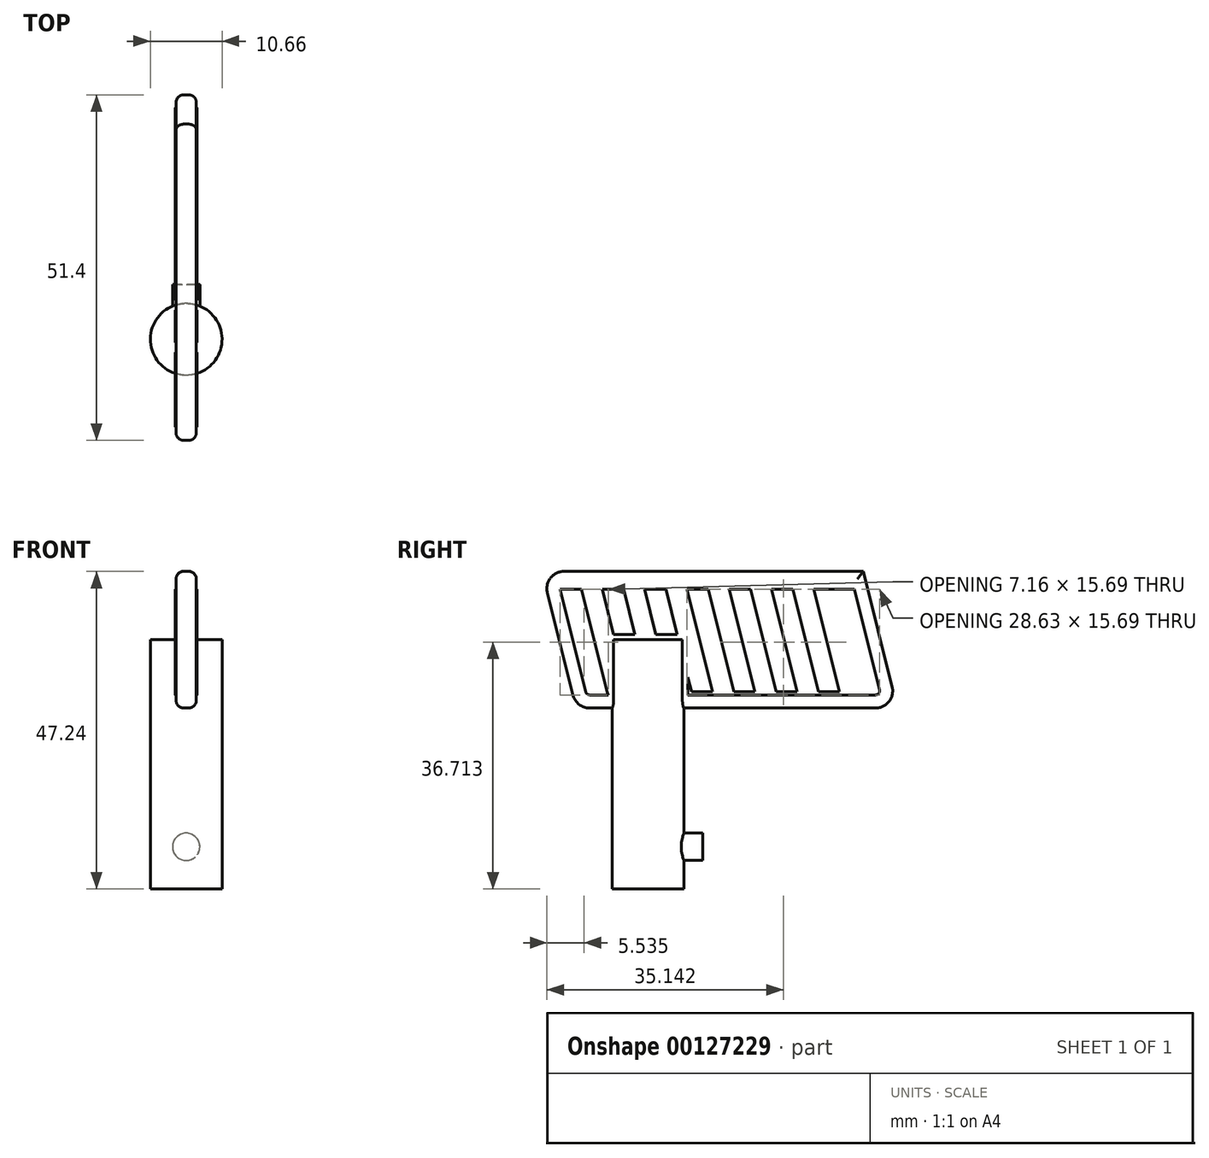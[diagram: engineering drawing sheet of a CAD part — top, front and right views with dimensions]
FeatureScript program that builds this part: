
annotation { "Feature Type Name" : "Feature", "Feature Type Description" : "" }
export const myFeature = defineFeature(function(context is Context, id is Id, definition is map)
    precondition{}
    {
        {
            var Q0;
            Q0=qCreatedBy(makeId("Top.planeOp"),FACE);
            var sketch = newSketch(context, id + "F0", { "sketchPlane" : qUnion([Q0])});
            skCircle(sketch, "E0", {"center": v(0, 0) * mm, "radius": 5.33 * mm});
            skSolve(sketch);
        }
        {
            var Q0;
            Q0 = qSketchRegion(id + "F0", true);
            extrude(context, id + "F1", {"entities" : qUnion([Q0]), "depth" : 37.08 * mm});
        }
        {
            var Q0;
            Q0=qCreatedBy(makeId("Front.planeOp"),FACE);
            var sketch = newSketch(context, id + "F2", { "sketchPlane" : qUnion([Q0])});
            skCircle(sketch, "E1", {"center": v(0, 6.27) * mm, "radius": 2.03 * mm});
            skSolve(sketch);
        }
        {
            var Q0;
            Q0 = qSketchRegion(id + "F2", true);
            extrude(context, id + "F3", {"entities" : qUnion([Q0]), "operationType" : NewBodyOperationType.ADD, "oppositeDirection" : true, "depth" : 8.13 * mm});
        }
        {
            var Q0;
            Q0=makeQuery(id+"F1.opExtrude","CAP_FACE",FACE,{"disambiguationData":[OSD([sQuery(id+"F0.wireOp",EDGE,"E0")])],"isStart":false});
            var sketch = newSketch(context, id + "F4", { "sketchPlane" : qUnion([Q0])});
            skLineSegment(sketch, "E2.bottom", {"start": v(-1.51, -10.67) * mm, "end": v(1.51, -10.67) * mm});
            skLineSegment(sketch, "E2.top", {"start": v(-1.51, 37.08) * mm, "end": v(1.51, 37.08) * mm});
            skLineSegment(sketch, "E2.left", {"start": v(-1.51, -10.67) * mm, "end": v(-1.51, 37.08) * mm});
            skLineSegment(sketch, "E2.right", {"start": v(1.51, -10.67) * mm, "end": v(1.51, 37.08) * mm});
            skSolve(sketch);
        }
        {
            var Q0;
            Q0 = qSketchRegion(id + "F4", true);
            extrude(context, id + "F5", {"entities" : qUnion([Q0]), "operationType" : NewBodyOperationType.ADD, "endBound" : BoundingType.SYMMETRIC, "depth" : 20.32 * mm});
        }
        {
            var Q0;
            Q0=makeQuery(id+"F5.opExtrude","SWEPT_FACE",FACE,{"disambiguationData":[OSD([sQuery(id+"F4.wireOp",EDGE,"E2.left")])]});
            var sketch = newSketch(context, id + "F6", { "sketchPlane" : qUnion([Q0])});
            skLineSegment(sketch, "E3", {"start": v(-37.08, 26.92) * mm, "end": v(-32, 47.24) * mm});
            skLineSegment(sketch, "E4", {"start": v(10.67, 26.92) * mm, "end": v(15.75, 47.24) * mm});
            skLineSegment(sketch, "E5", {"start": v(15.75, 47.24) * mm, "end": v(10.67, 47.24) * mm});
            skSolve(sketch);
        }
        {
            var Q0;
            Q0=makeQuery(id+"F6.imprint","IMPRINT",FACE,{"disambiguationData":[TD([[makeQuery(id+"F6.imprint","IMPRINT",EDGE,{"derivedFrom":sQuery(id+"F6.wireOp",EDGE,"E4")}),1.0]])]});
            var Q1;
            {var subQ0=sQuery(id+"F6.wireOp",EDGE,"E3");Q1=makeQuery(id+"F6.imprint","IMPRINT",FACE,{"disambiguationData":[TD([[makeQuery(id+"F6.imprint","IMPRINT",EDGE,{"derivedFrom":subQ0}),1.0]])]});}
            extrude(context, id + "F7", {"entities" : qUnion([Q0, Q1]), "operationType" : NewBodyOperationType.ADD, "oppositeDirection" : true, "depth" : 3.02 * mm});
        }
        {
            var Q0;
            {var subQ0=sQuery(id+"F4.wireOp",EDGE,"E2.left");Q0=makeQuery(id+"F7.boolean.opBoolean","MERGE",FACE,{"derivedFrom":[makeQuery(id+"F5.opExtrude","SWEPT_FACE",FACE,{"disambiguationData":[OSD([subQ0])]}),makeQuery(id+"F7.opExtrude","CAP_FACE",FACE,{"disambiguationData":[OSD([sQuery(id+"F4.wireOp",EDGE,"E2.bottom"),subQ0,sQuery(id+"F6.wireOp",EDGE,"E4"),sQuery(id+"F6.wireOp",EDGE,"E5")])],"isStart":true})]});}
            var sketch = newSketch(context, id + "F8", { "sketchPlane" : qUnion([Q0])});
            skLineSegment(sketch, "E6", {"start": v(-37.08, 26.92) * mm, "end": v(-32, 47.24) * mm});
            skSolve(sketch);
        }
        {
            var Q0;
            {var subQ0=sQuery(id+"F8.wireOp",EDGE,"E6");Q0=makeQuery(id+"F8.imprint","IMPRINT",FACE,{"disambiguationData":[TD([[makeQuery(id+"F8.imprint","IMPRINT",EDGE,{"derivedFrom":subQ0}),1.0]])]});}
            extrude(context, id + "F9", {"entities" : qUnion([Q0]), "operationType" : NewBodyOperationType.REMOVE, "endBound" : BoundingType.UP_TO_NEXT, "oppositeDirection" : true, "depth" : 25.4 * mm});
        }
        {
            var Q0;
            Q0=makeQuery(id+"F9.boolean.opBoolean","COPY",EDGE,{"derivedFrom":makeQuery(id+"F9.opExtrude","SWEPT_EDGE",EDGE,{"disambiguationData":[OSD([sQuery(id+"F4.wireOp",EDGE,"E2.left"),sQuery(id+"F6.wireOp",EDGE,"E5"),sQuery(id+"F8.wireOp",EDGE,"E6")])]})});
            var Q1;
            {var subQ0=sQuery(id+"F4.wireOp",EDGE,"E2.top");Q1=makeQuery(id+"F9.boolean.opBoolean","MERGE",EDGE,{"derivedFrom":[makeQuery(id+"F5.opExtrude","CAP_EDGE",EDGE,{"disambiguationData":[OSD([subQ0])],"isStart":true}),makeQuery(id+"F9.opExtrude","SWEPT_EDGE",EDGE,{"disambiguationData":[OSD([subQ0,sQuery(id+"F4.wireOp",EDGE,"E2.left"),sQuery(id+"F8.wireOp",EDGE,"E6")])]})]});}
            var Q2;
            Q2=makeQuery(id+"F7.opExtrude","SWEPT_EDGE",EDGE,{"disambiguationData":[OSD([sQuery(id+"F6.wireOp",EDGE,"E4"),sQuery(id+"F6.wireOp",EDGE,"E5")])]});
            var Q3;
            {var subQ0=sQuery(id+"F4.wireOp",EDGE,"E2.bottom");Q3=makeQuery(id+"F7.boolean.opBoolean","MERGE",EDGE,{"derivedFrom":[makeQuery(id+"F5.opExtrude","CAP_EDGE",EDGE,{"disambiguationData":[OSD([subQ0])],"isStart":true}),makeQuery(id+"F7.opExtrude","SWEPT_EDGE",EDGE,{"disambiguationData":[OSD([subQ0,sQuery(id+"F4.wireOp",EDGE,"E2.left"),sQuery(id+"F6.wireOp",EDGE,"E4")])]})]});}
            fillet(context, id + "F10", {"entities" : qUnion([Q0, Q1, Q2, Q3]), "radius" : 2.54 * mm, "tangentPropagation" : true, "allowEdgeOverflow" : false});
        }
        {
            var Q0;
            Q0=makeQuery(id+"F7.boolean.opBoolean","MERGE",EDGE,{"derivedFrom":[makeQuery(id+"F5.opExtrude","CAP_EDGE",EDGE,{"disambiguationData":[OSD([sQuery(id+"F4.wireOp",EDGE,"E2.left")])],"isStart":false}),makeQuery(id+"F7.opExtrude","CAP_EDGE",EDGE,{"disambiguationData":[OSD([sQuery(id+"F6.wireOp",EDGE,"E5")])],"isStart":true})]});
            var Q1;
            Q1=makeQuery(id+"F7.boolean.opBoolean","MERGE",EDGE,{"derivedFrom":[makeQuery(id+"F5.opExtrude","CAP_EDGE",EDGE,{"disambiguationData":[OSD([sQuery(id+"F4.wireOp",EDGE,"E2.right")])],"isStart":false}),makeQuery(id+"F7.opExtrude","CAP_EDGE",EDGE,{"disambiguationData":[OSD([sQuery(id+"F6.wireOp",EDGE,"E5")])],"isStart":false})]});
            var Q2;
            Q2=makeQuery(id+"F9.boolean.opBoolean","COPY",EDGE,{"derivedFrom":makeQuery(id+"F9.opExtrude","CAP_EDGE",EDGE,{"disambiguationData":[OSD([sQuery(id+"F8.wireOp",EDGE,"E6")])],"isStart":true})});
            var Q3;
            Q3=makeQuery(id+"F9.boolean.opBoolean","COPY",EDGE,{"derivedFrom":makeQuery(id+"F9.opExtrude","TWEAK_EDGE",EDGE,{"derivedFrom":[makeQuery(id+"F7.boolean.opBoolean","MERGE",FACE,{"derivedFrom":[makeQuery(id+"F5.opExtrude","SWEPT_FACE",FACE,{"disambiguationData":[OSD([sQuery(id+"F4.wireOp",EDGE,"E2.right")])]}),makeQuery(id+"F7.opExtrude","CAP_FACE",FACE,{"disambiguationData":[OSD([sQuery(id+"F4.wireOp",EDGE,"E2.bottom"),sQuery(id+"F4.wireOp",EDGE,"E2.left"),sQuery(id+"F6.wireOp",EDGE,"E4"),sQuery(id+"F6.wireOp",EDGE,"E5")])],"isStart":false})]}),makeQuery(id+"F8.imprint","IMPRINT",EDGE,{"derivedFrom":sQuery(id+"F8.wireOp",EDGE,"E6")})]})});
            var Q4;
            {var subQ0=sQuery(id+"F6.wireOp",EDGE,"E5");var subQ1=sQuery(id+"F4.wireOp",EDGE,"E2.left");Q4=makeQuery(id+"F10.opFillet","BLEND_EDGE",EDGE,{"blendedFrom":[makeQuery(id+"F9.boolean.opBoolean","COPY",EDGE,{"derivedFrom":makeQuery(id+"F9.opExtrude","SWEPT_EDGE",EDGE,{"disambiguationData":[OSD([subQ1,subQ0,sQuery(id+"F8.wireOp",EDGE,"E6")])]})}),makeQuery(id+"F7.boolean.opBoolean","MERGE",FACE,{"derivedFrom":[makeQuery(id+"F5.opExtrude","SWEPT_FACE",FACE,{"disambiguationData":[OSD([sQuery(id+"F4.wireOp",EDGE,"E2.right")])]}),makeQuery(id+"F7.opExtrude","CAP_FACE",FACE,{"disambiguationData":[OSD([sQuery(id+"F4.wireOp",EDGE,"E2.bottom"),subQ1,sQuery(id+"F6.wireOp",EDGE,"E4"),subQ0])],"isStart":false})]})],"blendedInto":[makeQuery(id+"F7.boolean.opBoolean","MERGE",FACE,{"derivedFrom":[makeQuery(id+"F5.opExtrude","SWEPT_FACE",FACE,{"disambiguationData":[OSD([sQuery(id+"F4.wireOp",EDGE,"E2.right")])]}),makeQuery(id+"F7.opExtrude","CAP_FACE",FACE,{"disambiguationData":[OSD([sQuery(id+"F4.wireOp",EDGE,"E2.bottom"),subQ1,sQuery(id+"F6.wireOp",EDGE,"E4"),subQ0])],"isStart":false})]})]});}
            var Q5;
            {var subQ0=sQuery(id+"F6.wireOp",EDGE,"E5");var subQ1=sQuery(id+"F4.wireOp",EDGE,"E2.left");Q5=makeQuery(id+"F10.opFillet","BLEND_EDGE",EDGE,{"blendedFrom":[makeQuery(id+"F9.boolean.opBoolean","COPY",EDGE,{"derivedFrom":makeQuery(id+"F9.opExtrude","SWEPT_EDGE",EDGE,{"disambiguationData":[OSD([subQ1,subQ0,sQuery(id+"F8.wireOp",EDGE,"E6")])]})}),makeQuery(id+"F7.boolean.opBoolean","MERGE",FACE,{"derivedFrom":[makeQuery(id+"F5.opExtrude","SWEPT_FACE",FACE,{"disambiguationData":[OSD([subQ1])]}),makeQuery(id+"F7.opExtrude","CAP_FACE",FACE,{"disambiguationData":[OSD([sQuery(id+"F4.wireOp",EDGE,"E2.bottom"),subQ1,sQuery(id+"F6.wireOp",EDGE,"E4"),subQ0])],"isStart":true})]})],"blendedInto":[makeQuery(id+"F7.boolean.opBoolean","MERGE",FACE,{"derivedFrom":[makeQuery(id+"F5.opExtrude","SWEPT_FACE",FACE,{"disambiguationData":[OSD([subQ1])]}),makeQuery(id+"F7.opExtrude","CAP_FACE",FACE,{"disambiguationData":[OSD([sQuery(id+"F4.wireOp",EDGE,"E2.bottom"),subQ1,sQuery(id+"F6.wireOp",EDGE,"E4"),subQ0])],"isStart":true})]})]});}
            var Q6;
            {var subQ0=sQuery(id+"F4.wireOp",EDGE,"E2.left");var subQ1=sQuery(id+"F4.wireOp",EDGE,"E2.top");Q6=makeQuery(id+"F10.opFillet","BLEND_EDGE",EDGE,{"blendedFrom":[makeQuery(id+"F9.boolean.opBoolean","MERGE",EDGE,{"derivedFrom":[makeQuery(id+"F5.opExtrude","CAP_EDGE",EDGE,{"disambiguationData":[OSD([subQ1])],"isStart":true}),makeQuery(id+"F9.opExtrude","SWEPT_EDGE",EDGE,{"disambiguationData":[OSD([subQ1,subQ0,sQuery(id+"F8.wireOp",EDGE,"E6")])]})]}),makeQuery(id+"F7.boolean.opBoolean","MERGE",FACE,{"derivedFrom":[makeQuery(id+"F5.opExtrude","SWEPT_FACE",FACE,{"disambiguationData":[OSD([subQ0])]}),makeQuery(id+"F7.opExtrude","CAP_FACE",FACE,{"disambiguationData":[OSD([sQuery(id+"F4.wireOp",EDGE,"E2.bottom"),subQ0,sQuery(id+"F6.wireOp",EDGE,"E4"),sQuery(id+"F6.wireOp",EDGE,"E5")])],"isStart":true})]})],"blendedInto":[makeQuery(id+"F7.boolean.opBoolean","MERGE",FACE,{"derivedFrom":[makeQuery(id+"F5.opExtrude","SWEPT_FACE",FACE,{"disambiguationData":[OSD([subQ0])]}),makeQuery(id+"F7.opExtrude","CAP_FACE",FACE,{"disambiguationData":[OSD([sQuery(id+"F4.wireOp",EDGE,"E2.bottom"),subQ0,sQuery(id+"F6.wireOp",EDGE,"E4"),sQuery(id+"F6.wireOp",EDGE,"E5")])],"isStart":true})]})]});}
            var Q7;
            {var subQ0=sQuery(id+"F4.wireOp",EDGE,"E2.left");var subQ1=sQuery(id+"F4.wireOp",EDGE,"E2.top");Q7=makeQuery(id+"F10.opFillet","BLEND_EDGE",EDGE,{"blendedFrom":[makeQuery(id+"F9.boolean.opBoolean","MERGE",EDGE,{"derivedFrom":[makeQuery(id+"F5.opExtrude","CAP_EDGE",EDGE,{"disambiguationData":[OSD([subQ1])],"isStart":true}),makeQuery(id+"F9.opExtrude","SWEPT_EDGE",EDGE,{"disambiguationData":[OSD([subQ1,subQ0,sQuery(id+"F8.wireOp",EDGE,"E6")])]})]}),makeQuery(id+"F7.boolean.opBoolean","MERGE",FACE,{"derivedFrom":[makeQuery(id+"F5.opExtrude","SWEPT_FACE",FACE,{"disambiguationData":[OSD([sQuery(id+"F4.wireOp",EDGE,"E2.right")])]}),makeQuery(id+"F7.opExtrude","CAP_FACE",FACE,{"disambiguationData":[OSD([sQuery(id+"F4.wireOp",EDGE,"E2.bottom"),subQ0,sQuery(id+"F6.wireOp",EDGE,"E4"),sQuery(id+"F6.wireOp",EDGE,"E5")])],"isStart":false})]})],"blendedInto":[makeQuery(id+"F7.boolean.opBoolean","MERGE",FACE,{"derivedFrom":[makeQuery(id+"F5.opExtrude","SWEPT_FACE",FACE,{"disambiguationData":[OSD([sQuery(id+"F4.wireOp",EDGE,"E2.right")])]}),makeQuery(id+"F7.opExtrude","CAP_FACE",FACE,{"disambiguationData":[OSD([sQuery(id+"F4.wireOp",EDGE,"E2.bottom"),subQ0,sQuery(id+"F6.wireOp",EDGE,"E4"),sQuery(id+"F6.wireOp",EDGE,"E5")])],"isStart":false})]})]});}
            var Q8;
            {var subQ0=sQuery(id+"F4.wireOp",EDGE,"E2.right");var subQ1=sQuery(id+"F4.wireOp",EDGE,"E2.top");Q8=makeQuery(id+"F5.boolean.opBoolean","SPLIT",EDGE,{"disambiguationData":[TD([makeQuery(id+"F5.opExtrude","SWEPT_FACE",FACE,{"disambiguationData":[OSD([subQ1])]})])],"derivedFrom":makeQuery(id+"F5.opExtrude","CAP_EDGE",EDGE,{"disambiguationData":[OSD([subQ0])],"isStart":true})});}
            var Q9;
            {var subQ0=sQuery(id+"F4.wireOp",EDGE,"E2.left");var subQ1=sQuery(id+"F4.wireOp",EDGE,"E2.top");Q9=makeQuery(id+"F5.boolean.opBoolean","SPLIT",EDGE,{"disambiguationData":[TD([makeQuery(id+"F5.opExtrude","SWEPT_FACE",FACE,{"disambiguationData":[OSD([subQ1])]})])],"derivedFrom":makeQuery(id+"F5.opExtrude","CAP_EDGE",EDGE,{"disambiguationData":[OSD([subQ0])],"isStart":true})});}
            var Q10;
            {var subQ0=sQuery(id+"F6.wireOp",EDGE,"E5");var subQ1=sQuery(id+"F6.wireOp",EDGE,"E4");Q10=makeQuery(id+"F10.opFillet","BLEND_EDGE",EDGE,{"blendedFrom":[makeQuery(id+"F7.opExtrude","SWEPT_EDGE",EDGE,{"disambiguationData":[OSD([subQ1,subQ0])]}),makeQuery(id+"F7.boolean.opBoolean","MERGE",FACE,{"derivedFrom":[makeQuery(id+"F5.opExtrude","SWEPT_FACE",FACE,{"disambiguationData":[OSD([sQuery(id+"F4.wireOp",EDGE,"E2.right")])]}),makeQuery(id+"F7.opExtrude","CAP_FACE",FACE,{"disambiguationData":[OSD([sQuery(id+"F4.wireOp",EDGE,"E2.bottom"),sQuery(id+"F4.wireOp",EDGE,"E2.left"),subQ1,subQ0])],"isStart":false})]})],"blendedInto":[makeQuery(id+"F7.boolean.opBoolean","MERGE",FACE,{"derivedFrom":[makeQuery(id+"F5.opExtrude","SWEPT_FACE",FACE,{"disambiguationData":[OSD([sQuery(id+"F4.wireOp",EDGE,"E2.right")])]}),makeQuery(id+"F7.opExtrude","CAP_FACE",FACE,{"disambiguationData":[OSD([sQuery(id+"F4.wireOp",EDGE,"E2.bottom"),sQuery(id+"F4.wireOp",EDGE,"E2.left"),subQ1,subQ0])],"isStart":false})]})]});}
            var Q11;
            Q11=makeQuery(id+"F7.opExtrude","CAP_EDGE",EDGE,{"disambiguationData":[OSD([sQuery(id+"F6.wireOp",EDGE,"E4")])],"isStart":false});
            var Q12;
            {var subQ0=sQuery(id+"F6.wireOp",EDGE,"E5");var subQ1=sQuery(id+"F6.wireOp",EDGE,"E4");var subQ2=sQuery(id+"F4.wireOp",EDGE,"E2.left");Q12=makeQuery(id+"F10.opFillet","BLEND_EDGE",EDGE,{"blendedFrom":[makeQuery(id+"F7.opExtrude","SWEPT_EDGE",EDGE,{"disambiguationData":[OSD([subQ1,subQ0])]}),makeQuery(id+"F7.boolean.opBoolean","MERGE",FACE,{"derivedFrom":[makeQuery(id+"F5.opExtrude","SWEPT_FACE",FACE,{"disambiguationData":[OSD([subQ2])]}),makeQuery(id+"F7.opExtrude","CAP_FACE",FACE,{"disambiguationData":[OSD([sQuery(id+"F4.wireOp",EDGE,"E2.bottom"),subQ2,subQ1,subQ0])],"isStart":true})]})],"blendedInto":[makeQuery(id+"F7.boolean.opBoolean","MERGE",FACE,{"derivedFrom":[makeQuery(id+"F5.opExtrude","SWEPT_FACE",FACE,{"disambiguationData":[OSD([subQ2])]}),makeQuery(id+"F7.opExtrude","CAP_FACE",FACE,{"disambiguationData":[OSD([sQuery(id+"F4.wireOp",EDGE,"E2.bottom"),subQ2,subQ1,subQ0])],"isStart":true})]})]});}
            var Q13;
            Q13=makeQuery(id+"F7.opExtrude","CAP_EDGE",EDGE,{"disambiguationData":[OSD([sQuery(id+"F6.wireOp",EDGE,"E4")])],"isStart":true});
            var Q14;
            {var subQ0=sQuery(id+"F6.wireOp",EDGE,"E4");var subQ1=sQuery(id+"F4.wireOp",EDGE,"E2.left");var subQ2=sQuery(id+"F4.wireOp",EDGE,"E2.bottom");Q14=makeQuery(id+"F10.opFillet","BLEND_EDGE",EDGE,{"blendedFrom":[makeQuery(id+"F7.boolean.opBoolean","MERGE",EDGE,{"derivedFrom":[makeQuery(id+"F5.opExtrude","CAP_EDGE",EDGE,{"disambiguationData":[OSD([subQ2])],"isStart":true}),makeQuery(id+"F7.opExtrude","SWEPT_EDGE",EDGE,{"disambiguationData":[OSD([subQ2,subQ1,subQ0])]})]}),makeQuery(id+"F7.boolean.opBoolean","MERGE",FACE,{"derivedFrom":[makeQuery(id+"F5.opExtrude","SWEPT_FACE",FACE,{"disambiguationData":[OSD([sQuery(id+"F4.wireOp",EDGE,"E2.right")])]}),makeQuery(id+"F7.opExtrude","CAP_FACE",FACE,{"disambiguationData":[OSD([subQ2,subQ1,subQ0,sQuery(id+"F6.wireOp",EDGE,"E5")])],"isStart":false})]})],"blendedInto":[makeQuery(id+"F7.boolean.opBoolean","MERGE",FACE,{"derivedFrom":[makeQuery(id+"F5.opExtrude","SWEPT_FACE",FACE,{"disambiguationData":[OSD([sQuery(id+"F4.wireOp",EDGE,"E2.right")])]}),makeQuery(id+"F7.opExtrude","CAP_FACE",FACE,{"disambiguationData":[OSD([subQ2,subQ1,subQ0,sQuery(id+"F6.wireOp",EDGE,"E5")])],"isStart":false})]})]});}
            var Q15;
            {var subQ0=sQuery(id+"F4.wireOp",EDGE,"E2.bottom");var subQ1=sQuery(id+"F4.wireOp",EDGE,"E2.right");Q15=makeQuery(id+"F5.boolean.opBoolean","SPLIT",EDGE,{"disambiguationData":[TD([makeQuery(id+"F5.opExtrude","SWEPT_FACE",FACE,{"disambiguationData":[OSD([subQ0])]})])],"derivedFrom":makeQuery(id+"F5.opExtrude","CAP_EDGE",EDGE,{"disambiguationData":[OSD([subQ1])],"isStart":true})});}
            var Q16;
            {var subQ0=sQuery(id+"F4.wireOp",EDGE,"E2.bottom");var subQ1=sQuery(id+"F4.wireOp",EDGE,"E2.left");Q16=makeQuery(id+"F5.boolean.opBoolean","SPLIT",EDGE,{"disambiguationData":[TD([makeQuery(id+"F5.opExtrude","SWEPT_FACE",FACE,{"disambiguationData":[OSD([subQ0])]})])],"derivedFrom":makeQuery(id+"F5.opExtrude","CAP_EDGE",EDGE,{"disambiguationData":[OSD([subQ1])],"isStart":true})});}
            var Q17;
            {var subQ0=sQuery(id+"F6.wireOp",EDGE,"E4");var subQ1=sQuery(id+"F4.wireOp",EDGE,"E2.left");var subQ2=sQuery(id+"F4.wireOp",EDGE,"E2.bottom");Q17=makeQuery(id+"F10.opFillet","BLEND_EDGE",EDGE,{"blendedFrom":[makeQuery(id+"F7.boolean.opBoolean","MERGE",EDGE,{"derivedFrom":[makeQuery(id+"F5.opExtrude","CAP_EDGE",EDGE,{"disambiguationData":[OSD([subQ2])],"isStart":true}),makeQuery(id+"F7.opExtrude","SWEPT_EDGE",EDGE,{"disambiguationData":[OSD([subQ2,subQ1,subQ0])]})]}),makeQuery(id+"F7.boolean.opBoolean","MERGE",FACE,{"derivedFrom":[makeQuery(id+"F5.opExtrude","SWEPT_FACE",FACE,{"disambiguationData":[OSD([subQ1])]}),makeQuery(id+"F7.opExtrude","CAP_FACE",FACE,{"disambiguationData":[OSD([subQ2,subQ1,subQ0,sQuery(id+"F6.wireOp",EDGE,"E5")])],"isStart":true})]})],"blendedInto":[makeQuery(id+"F7.boolean.opBoolean","MERGE",FACE,{"derivedFrom":[makeQuery(id+"F5.opExtrude","SWEPT_FACE",FACE,{"disambiguationData":[OSD([subQ1])]}),makeQuery(id+"F7.opExtrude","CAP_FACE",FACE,{"disambiguationData":[OSD([subQ2,subQ1,subQ0,sQuery(id+"F6.wireOp",EDGE,"E5")])],"isStart":true})]})]});}
            fillet(context, id + "F11", {"entities" : qUnion([Q0, Q1, Q2, Q3, Q4, Q5, Q6, Q7, Q8, Q9, Q10, Q11, Q12, Q13, Q14, Q15, Q16, Q17]), "radius" : 1.14 * mm, "tangentPropagation" : true, "allowEdgeOverflow" : false});
        }
        {
            var Q0;
            Q0=makeQuery(id+"F7.boolean.opBoolean","MERGE",FACE,{"derivedFrom":[makeQuery(id+"F5.opExtrude","SWEPT_FACE",FACE,{"disambiguationData":[OSD([sQuery(id+"F4.wireOp",EDGE,"E2.right")])]}),makeQuery(id+"F7.opExtrude","CAP_FACE",FACE,{"disambiguationData":[OSD([sQuery(id+"F4.wireOp",EDGE,"E2.bottom"),sQuery(id+"F4.wireOp",EDGE,"E2.left"),sQuery(id+"F6.wireOp",EDGE,"E4"),sQuery(id+"F6.wireOp",EDGE,"E5")])],"isStart":false})]});
            var sketch = newSketch(context, id + "F12", { "sketchPlane" : qUnion([Q0])});
            skLineSegment(sketch, "E7.0", {"start": v(-13.07, 44.56) * mm, "end": v(-9.26, 29.32) * mm});
            skLineSegment(sketch, "E7.1", {"start": v(5.92, 37.88) * mm, "end": v(5.92, 28.87) * mm});
            skLineSegment(sketch, "E7.2", {"start": v(-5.92, 37.88) * mm, "end": v(4.32, 37.88) * mm});
            skLineSegment(sketch, "E7.3", {"start": v(-5.92, 28.87) * mm, "end": v(-5.92, 37.88) * mm});
            skLineSegment(sketch, "E7.4", {"start": v(-8.68, 28.87) * mm, "end": v(-5.92, 28.87) * mm});
            skLineSegment(sketch, "E7.5", {"start": v(5.92, 28.87) * mm, "end": v(33.83, 28.87) * mm});
            skArc(sketch, "E7.6", {"start": v(-9.26, 29.32) * mm, "mid": v(-9.05, 29) * mm, "end": v(-8.68, 28.87) * mm});
            skArc(sketch, "E7.7", {"start": v(33.83, 28.87) * mm, "mid": v(34.3, 29.1) * mm, "end": v(34.4, 29.6) * mm});
            skLineSegment(sketch, "E7.8", {"start": v(34.4, 29.6) * mm, "end": v(30.6, 44.85) * mm});
            skArc(sketch, "E7.9", {"start": v(30.6, 44.85) * mm, "mid": v(30.39, 45.17) * mm, "end": v(30.02, 45.3) * mm});
            skLineSegment(sketch, "E7.10", {"start": v(30.02, 45.3) * mm, "end": v(-12.5, 45.3) * mm});
            skArc(sketch, "E7.11", {"start": v(-12.5, 45.3) * mm, "mid": v(-12.97, 45.07) * mm, "end": v(-13.07, 44.56) * mm});
            skLineSegment(sketch, "E8.1.0.0", {"start": v(-9.93, 44.56) * mm, "end": v(-6.12, 29.32) * mm});
            skLineSegment(sketch, "E8.2.0.0", {"start": v(-6.78, 44.56) * mm, "end": v(-5.11, 37.88) * mm});
            skLineSegment(sketch, "E8.3.0.0", {"start": v(-3.64, 44.56) * mm, "end": v(-1.97, 37.88) * mm});
            skLineSegment(sketch, "E8.4.0.0", {"start": v(-0.5, 44.56) * mm, "end": v(1.18, 37.88) * mm});
            skLineSegment(sketch, "E8.5.0.0", {"start": v(2.65, 44.56) * mm, "end": v(4.32, 37.88) * mm});
            skLineSegment(sketch, "E8.6.0.0", {"start": v(5.8, 44.56) * mm, "end": v(9.6, 29.32) * mm});
            skLineSegment(sketch, "E8.7.0.0", {"start": v(8.94, 44.56) * mm, "end": v(12.75, 29.32) * mm});
            skLineSegment(sketch, "E8.8.0.0", {"start": v(12.09, 44.56) * mm, "end": v(15.9, 29.32) * mm});
            skLineSegment(sketch, "E8.9.0.0", {"start": v(15.23, 44.56) * mm, "end": v(19.04, 29.32) * mm});
            skLineSegment(sketch, "E8.10.0.0", {"start": v(18.38, 44.56) * mm, "end": v(22.19, 29.32) * mm});
            skLineSegment(sketch, "E8.11.0.0", {"start": v(21.52, 44.56) * mm, "end": v(25.33, 29.32) * mm});
            skLineSegment(sketch, "E8.12.0.0", {"start": v(24.67, 44.56) * mm, "end": v(28.48, 29.32) * mm});
            skLineSegment(sketch, "E8.13.0.0", {"start": v(27.81, 44.56) * mm, "end": v(31.62, 29.32) * mm});
            skLineSegment(sketch, "E8.direction1", {"start": v(-9.26, 29.32) * mm, "end": v(-6.12, 29.32) * mm, "construction": true});
            skLineSegment(sketch, "E9", {"start": v(4.32, 37.88) * mm, "end": v(5.92, 37.88) * mm});
            skLineSegment(sketch, "E10", {"start": v(5.92, 31.5) * mm, "end": v(6.46, 29.32) * mm});
            skLineSegment(sketch, "E11", {"start": v(-13.07, 44.56) * mm, "end": v(30.67, 44.56) * mm});
            skLineSegment(sketch, "E12", {"start": v(30.67, 44.56) * mm, "end": v(34.4, 29.6) * mm});
            skLineSegment(sketch, "E13", {"start": v(31.62, 29.32) * mm, "end": v(6.46, 29.32) * mm});
            skLineSegment(sketch, "E14", {"start": v(31.62, 29.32) * mm, "end": v(33.83, 29.46) * mm});
            skLineSegment(sketch, "E15", {"start": v(34.4, 29.6) * mm, "end": v(33.83, 29.46) * mm});
            skLineSegment(sketch, "E16", {"start": v(-9.26, 29.32) * mm, "end": v(-6.12, 29.32) * mm});
            skLineSegment(sketch, "E17", {"start": v(-6.12, 29.32) * mm, "end": v(-5.92, 28.87) * mm});
            skSolve(sketch);
        }
        {
            var Q0;
            Q0=makeQuery(id+"F12.imprint","IMPRINT",FACE,{"disambiguationData":[TD([[makeQuery(id+"F12.imprint","IMPRINT",EDGE,{"derivedFrom":sQuery(id+"F12.wireOp",EDGE,"E7.4")}),1.0]])]});
            var Q1;
            {var subQ0=sQuery(id+"F12.wireOp",EDGE,"E7.0");Q1=makeQuery(id+"F12.imprint","IMPRINT",FACE,{"disambiguationData":[TD([[makeQuery(id+"F12.imprint","IMPRINT",EDGE,{"derivedFrom":subQ0}),1.0]])]});}
            var Q2;
            {var subQ0=sQuery(id+"F12.wireOp",EDGE,"E8.2.0.0");Q2=makeQuery(id+"F12.imprint","IMPRINT",FACE,{"disambiguationData":[TD([[makeQuery(id+"F12.imprint","IMPRINT",EDGE,{"derivedFrom":subQ0}),1.0]])]});}
            var Q3;
            {var subQ2=sQuery(id+"F12.wireOp",EDGE,"E8.4.0.0");Q3=makeQuery(id+"F12.imprint","IMPRINT",FACE,{"disambiguationData":[TD([[makeQuery(id+"F12.imprint","IMPRINT",EDGE,{"derivedFrom":subQ2}),1.0]])]});}
            var Q4;
            {var subQ5=sQuery(id+"F12.wireOp",EDGE,"E7.5");Q4=makeQuery(id+"F12.imprint","IMPRINT",FACE,{"disambiguationData":[TD([[makeQuery(id+"F12.imprint","IMPRINT",EDGE,{"derivedFrom":subQ5}),1.0]])]});}
            var Q5;
            {var subQ8=sQuery(id+"F12.wireOp",EDGE,"E7.8");Q5=makeQuery(id+"F12.imprint","IMPRINT",FACE,{"disambiguationData":[TD([[makeQuery(id+"F12.imprint","IMPRINT",EDGE,{"derivedFrom":subQ8}),1.0]])]});}
            var Q6;
            {var subQ0=sQuery(id+"F12.wireOp",EDGE,"E8.6.0.0");Q6=makeQuery(id+"F12.imprint","IMPRINT",FACE,{"disambiguationData":[TD([[makeQuery(id+"F12.imprint","IMPRINT",EDGE,{"derivedFrom":subQ0}),1.0]])]});}
            var Q7;
            {var subQ0=sQuery(id+"F12.wireOp",EDGE,"E8.8.0.0");Q7=makeQuery(id+"F12.imprint","IMPRINT",FACE,{"disambiguationData":[TD([[makeQuery(id+"F12.imprint","IMPRINT",EDGE,{"derivedFrom":subQ0}),1.0]])]});}
            var Q8;
            {var subQ0=sQuery(id+"F12.wireOp",EDGE,"E8.10.0.0");Q8=makeQuery(id+"F12.imprint","IMPRINT",FACE,{"disambiguationData":[TD([[makeQuery(id+"F12.imprint","IMPRINT",EDGE,{"derivedFrom":subQ0}),1.0]])]});}
            var Q9;
            {var subQ0=sQuery(id+"F12.wireOp",EDGE,"E8.12.0.0");Q9=makeQuery(id+"F12.imprint","IMPRINT",FACE,{"disambiguationData":[TD([[makeQuery(id+"F12.imprint","IMPRINT",EDGE,{"derivedFrom":subQ0}),1.0]])]});}
            extrude(context, id + "F13", {"entities" : qUnion([Q0, Q1, Q2, Q3, Q4, Q5, Q6, Q7, Q8, Q9]), "operationType" : NewBodyOperationType.ADD, "depth" : 0.13 * mm});
        }
        {
            var Q0;
            Q0=makeQuery(id+"F1.opExtrude","SWEPT_BODY",BODY,{"disambiguationData":[OSD([sQuery(id+"F0.wireOp",EDGE,"E0")])]});
            var Q1;
            Q1=qCreatedBy(makeId("Right.planeOp"),FACE);
            mirror(context, id + "F14", {"operationType" : NewBodyOperationType.ADD, "entities" : qUnion([Q0]), "mirrorPlane" : qUnion([Q1])});
        }
        {
            var Q0;
            Q0=makeQuery(id+"F13.opExtrude","CAP_EDGE",EDGE,{"disambiguationData":[OSD([sQuery(id+"F12.wireOp",EDGE,"E8.1.0.0")])],"isStart":false});
            var Q1;
            Q1=makeQuery(id+"F13.opExtrude","CAP_EDGE",EDGE,{"disambiguationData":[OSD([sQuery(id+"F12.wireOp",EDGE,"E8.2.0.0")])],"isStart":false});
            var Q2;
            Q2=makeQuery(id+"F13.opExtrude","CAP_EDGE",EDGE,{"disambiguationData":[OSD([sQuery(id+"F12.wireOp",EDGE,"E8.3.0.0")])],"isStart":false});
            var Q3;
            Q3=makeQuery(id+"F13.opExtrude","CAP_EDGE",EDGE,{"disambiguationData":[OSD([sQuery(id+"F12.wireOp",EDGE,"E8.4.0.0")])],"isStart":false});
            var Q4;
            Q4=makeQuery(id+"F13.opExtrude","CAP_EDGE",EDGE,{"disambiguationData":[OSD([sQuery(id+"F12.wireOp",EDGE,"E8.5.0.0")])],"isStart":false});
            var Q5;
            Q5=makeQuery(id+"F13.opExtrude","CAP_EDGE",EDGE,{"disambiguationData":[OSD([sQuery(id+"F12.wireOp",EDGE,"E8.6.0.0")])],"isStart":false});
            var Q6;
            Q6=makeQuery(id+"F13.opExtrude","CAP_EDGE",EDGE,{"disambiguationData":[OSD([sQuery(id+"F12.wireOp",EDGE,"E8.7.0.0")])],"isStart":false});
            var Q7;
            Q7=makeQuery(id+"F13.opExtrude","CAP_EDGE",EDGE,{"disambiguationData":[OSD([sQuery(id+"F12.wireOp",EDGE,"E8.8.0.0")])],"isStart":false});
            var Q8;
            Q8=makeQuery(id+"F13.opExtrude","CAP_EDGE",EDGE,{"disambiguationData":[OSD([sQuery(id+"F12.wireOp",EDGE,"E8.9.0.0")])],"isStart":false});
            var Q9;
            Q9=makeQuery(id+"F13.opExtrude","CAP_EDGE",EDGE,{"disambiguationData":[OSD([sQuery(id+"F12.wireOp",EDGE,"E8.10.0.0")])],"isStart":false});
            var Q10;
            Q10=makeQuery(id+"F13.opExtrude","CAP_EDGE",EDGE,{"disambiguationData":[OSD([sQuery(id+"F12.wireOp",EDGE,"E8.11.0.0")])],"isStart":false});
            var Q11;
            Q11=makeQuery(id+"F13.opExtrude","CAP_EDGE",EDGE,{"disambiguationData":[OSD([sQuery(id+"F12.wireOp",EDGE,"E8.12.0.0")])],"isStart":false});
            var Q12;
            Q12=makeQuery(id+"F13.opExtrude","CAP_EDGE",EDGE,{"disambiguationData":[OSD([sQuery(id+"F12.wireOp",EDGE,"E8.13.0.0")])],"isStart":false});
            chamfer(context, id + "F15", {"entities" : qUnion([Q0, Q1, Q2, Q3, Q4, Q5, Q6, Q7, Q8, Q9, Q10, Q11, Q12]), "width" : 0.5 * mm, "tangentPropagation" : true});
        }
        {
            var Q0;
            {var subQ0=sQuery(id+"F0.wireOp",EDGE,"E0");Q0=makeQuery(id+"F5.boolean.opBoolean","SPLIT",EDGE,{"disambiguationData":[TD([makeQuery(id+"F5.opExtrude","SWEPT_FACE",FACE,{"disambiguationData":[OSD([sQuery(id+"F4.wireOp",EDGE,"E2.right")])]})])],"derivedFrom":makeQuery(id+"F1.opExtrude","CAP_EDGE",EDGE,{"disambiguationData":[OSD([subQ0])],"isStart":false})});}
            chamfer(context, id + "F16", {"entities" : qUnion([Q0]), "width" : 2.54 * mm, "tangentPropagation" : true});
        }
        {
            var Q0;
            Q0=makeQuery(id+"F1.opExtrude","SWEPT_BODY",BODY,{"disambiguationData":[OSD([sQuery(id+"F0.wireOp",EDGE,"E0")])]});
            var Q1;
            Q1=qCreatedBy(makeId("Right.planeOp"),FACE);
            mirror(context, id + "F17", {"operationType" : NewBodyOperationType.ADD, "entities" : qUnion([Q0]), "mirrorPlane" : qUnion([Q1])});
        }
    });
